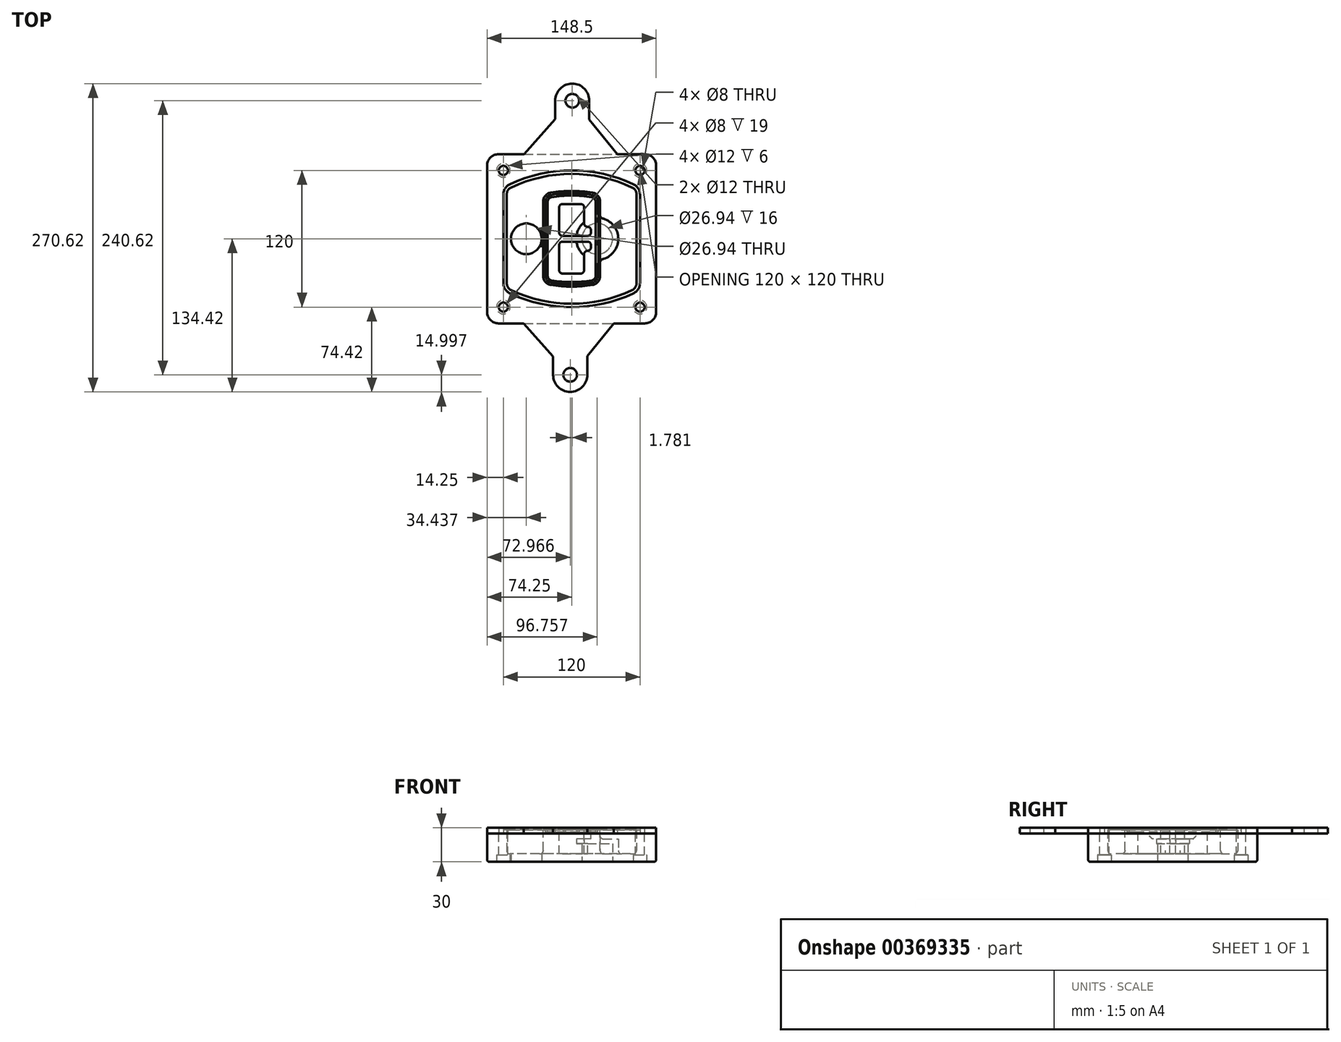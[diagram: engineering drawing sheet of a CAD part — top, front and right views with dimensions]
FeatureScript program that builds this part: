
annotation { "Feature Type Name" : "Feature", "Feature Type Description" : "" }
export const myFeature = defineFeature(function(context is Context, id is Id, definition is map)
    precondition{}
    {
        {
            var Q0;
            Q0=qCreatedBy(makeId("Top.planeOp"),FACE);
            var sketch = newSketch(context, id + "F0", { "sketchPlane" : qUnion([Q0])});
            skPoint(sketch, "E0.rect.middle", {"position": v(0, 0) * mm});
            skLineSegment(sketch, "E1.bottom", {"start": v(-64.25, -74.25) * mm, "end": v(64.25, -74.25) * mm});
            skLineSegment(sketch, "E1.top", {"start": v(-64.25, 74.25) * mm, "end": v(64.25, 74.25) * mm});
            skLineSegment(sketch, "E1.left", {"start": v(-74.25, -64.25) * mm, "end": v(-74.25, 64.25) * mm});
            skLineSegment(sketch, "E1.right", {"start": v(74.25, -64.25) * mm, "end": v(74.25, 64.25) * mm});
            skLineSegment(sketch, "E2", {"start": v(-74.25, 74.25) * mm, "end": v(74.25, -74.25) * mm, "construction": true});
            skLineSegment(sketch, "E3", {"start": v(74.25, 74.25) * mm, "end": v(-74.25, -74.25) * mm, "construction": true});
            skCircle(sketch, "E4", {"center": v(-60, 60) * mm, "radius": 4 * mm});
            skCircle(sketch, "E5", {"center": v(60, 60) * mm, "radius": 4 * mm});
            skCircle(sketch, "E6", {"center": v(60, -60) * mm, "radius": 4 * mm});
            skCircle(sketch, "E7", {"center": v(-60, -60) * mm, "radius": 4 * mm});
            skLineSegment(sketch, "E8", {"start": v(-60, 60) * mm, "end": v(60, 60) * mm, "construction": true});
            skLineSegment(sketch, "E9", {"start": v(60, 60) * mm, "end": v(60, -60) * mm, "construction": true});
            skLineSegment(sketch, "E10", {"start": v(60, -60) * mm, "end": v(-60, -60) * mm, "construction": true});
            skLineSegment(sketch, "E11", {"start": v(-60, -60) * mm, "end": v(-60, 60) * mm, "construction": true});
            skLineSegment(sketch, "E12", {"start": v(-60, 38.83) * mm, "end": v(-60, -38.83) * mm});
            skLineSegment(sketch, "E13", {"start": v(60, 38.83) * mm, "end": v(60, -38.83) * mm});
            skArc(sketch, "E14", {"start": v(54.26, 47.88) * mm, "mid": v(0, 60) * mm, "end": v(-54.26, 47.88) * mm});
            skArc(sketch, "E15", {"start": v(-54.26, -47.88) * mm, "mid": v(0, -60) * mm, "end": v(54.26, -47.88) * mm});
            skLineSegment(sketch, "E16", {"start": v(-60, 0) * mm, "end": v(60, 0) * mm, "construction": true});
            skPoint(sketch, "E17.visualSharp", {"position": v(-60, -45) * mm});
            skArc(sketch, "E17.filletArc", {"start": v(-60, -38.83) * mm, "mid": v(-58.44, -44.2) * mm, "end": v(-54.26, -47.88) * mm});
            skPoint(sketch, "E18.visualSharp", {"position": v(-60, 45) * mm});
            skArc(sketch, "E18.filletArc", {"start": v(-54.26, 47.88) * mm, "mid": v(-58.44, 44.2) * mm, "end": v(-60, 38.83) * mm});
            skPoint(sketch, "E19.visualSharp", {"position": v(60, 45) * mm});
            skArc(sketch, "E19.filletArc", {"start": v(60, 38.83) * mm, "mid": v(58.44, 44.2) * mm, "end": v(54.26, 47.88) * mm});
            skPoint(sketch, "E20.visualSharp", {"position": v(60, -45) * mm});
            skArc(sketch, "E20.filletArc", {"start": v(54.26, -47.88) * mm, "mid": v(58.44, -44.2) * mm, "end": v(60, -38.83) * mm});
            skPoint(sketch, "E21.visualSharp", {"position": v(-74.25, 74.25) * mm});
            skArc(sketch, "E21.filletArc", {"start": v(-64.25, 74.25) * mm, "mid": v(-71.32, 71.32) * mm, "end": v(-74.25, 64.25) * mm});
            skPoint(sketch, "E22.visualSharp", {"position": v(74.25, 74.25) * mm});
            skArc(sketch, "E22.filletArc", {"start": v(74.25, 64.25) * mm, "mid": v(71.32, 71.32) * mm, "end": v(64.25, 74.25) * mm});
            skPoint(sketch, "E23.visualSharp", {"position": v(74.25, -74.25) * mm});
            skArc(sketch, "E23.filletArc", {"start": v(64.25, -74.25) * mm, "mid": v(71.32, -71.32) * mm, "end": v(74.25, -64.25) * mm});
            skPoint(sketch, "E24.visualSharp", {"position": v(-74.25, -74.25) * mm});
            skArc(sketch, "E24.filletArc", {"start": v(-74.25, -64.25) * mm, "mid": v(-71.32, -71.32) * mm, "end": v(-64.25, -74.25) * mm});
            skArc(sketch, "E25.0", {"start": v(57, 38.83) * mm, "mid": v(55.9, 42.58) * mm, "end": v(52.98, 45.17) * mm});
            skLineSegment(sketch, "E25.1", {"start": v(57, 38.83) * mm, "end": v(57, -38.83) * mm});
            skArc(sketch, "E25.2", {"start": v(52.98, -45.17) * mm, "mid": v(55.9, -42.58) * mm, "end": v(57, -38.83) * mm});
            skArc(sketch, "E25.3", {"start": v(-52.98, -45.17) * mm, "mid": v(0, -57) * mm, "end": v(52.98, -45.17) * mm});
            skArc(sketch, "E25.4", {"start": v(-57, -38.83) * mm, "mid": v(-55.9, -42.58) * mm, "end": v(-52.98, -45.17) * mm});
            skArc(sketch, "E25.5", {"start": v(52.98, 45.17) * mm, "mid": v(0, 57) * mm, "end": v(-52.98, 45.17) * mm});
            skLineSegment(sketch, "E25.6", {"start": v(-57, 38.83) * mm, "end": v(-57, -38.83) * mm});
            skArc(sketch, "E25.7", {"start": v(-52.98, 45.17) * mm, "mid": v(-55.9, 42.58) * mm, "end": v(-57, 38.83) * mm});
            skArc(sketch, "E26.0", {"start": v(-55.96, 51.5) * mm, "mid": v(-61.82, 46.33) * mm, "end": v(-64, 38.83) * mm});
            skArc(sketch, "E26.1", {"start": v(55.96, 51.5) * mm, "mid": v(0, 64) * mm, "end": v(-55.96, 51.5) * mm});
            skArc(sketch, "E26.2", {"start": v(64, 38.83) * mm, "mid": v(61.82, 46.33) * mm, "end": v(55.96, 51.5) * mm});
            skLineSegment(sketch, "E26.3", {"start": v(64, 38.83) * mm, "end": v(64, -38.83) * mm});
            skArc(sketch, "E26.4", {"start": v(55.96, -51.5) * mm, "mid": v(61.82, -46.33) * mm, "end": v(64, -38.83) * mm});
            skLineSegment(sketch, "E26.5", {"start": v(-64, 38.83) * mm, "end": v(-64, -38.83) * mm});
            skArc(sketch, "E26.6", {"start": v(-55.96, -51.5) * mm, "mid": v(0, -64) * mm, "end": v(55.96, -51.5) * mm});
            skArc(sketch, "E26.7", {"start": v(-64, -38.83) * mm, "mid": v(-61.82, -46.33) * mm, "end": v(-55.96, -51.5) * mm});
            skSolve(sketch);
        }
        {
            var Q0;
            Q0=makeQuery(id+"F0.imprint","IMPRINT",FACE,{"disambiguationData":[TD([[makeQuery(id+"F0.imprint","IMPRINT",EDGE,{"derivedFrom":sQuery(id+"F0.wireOp",EDGE,"E1.bottom")}),1.0]])]});
            var Q1;
            Q1=makeQuery(id+"F0.imprint","IMPRINT",FACE,{"disambiguationData":[TD([[makeQuery(id+"F0.imprint","IMPRINT",EDGE,{"derivedFrom":sQuery(id+"F0.wireOp",EDGE,"E12")}),1.0]])]});
            var Q2;
            Q2=makeQuery(id+"F0.imprint","IMPRINT",FACE,{"disambiguationData":[TD([[makeQuery(id+"F0.imprint","IMPRINT",EDGE,{"derivedFrom":sQuery(id+"F0.wireOp",EDGE,"E25.0")}),1.0]])]});
            var Q3;
            Q3=makeQuery(id+"F0.imprint","IMPRINT",FACE,{"disambiguationData":[TD([[makeQuery(id+"F0.imprint","IMPRINT",EDGE,{"derivedFrom":sQuery(id+"F0.wireOp",EDGE,"E12")}),-1.0]])]});
            extrude(context, id + "F1", {"entities" : qUnion([Q0, Q1, Q2, Q3]), "oppositeDirection" : true, "depth" : 25 * mm});
        }
        {
            var Q0;
            Q0=makeQuery(id+"F0.imprint","IMPRINT",FACE,{"disambiguationData":[TD([[makeQuery(id+"F0.imprint","IMPRINT",EDGE,{"derivedFrom":sQuery(id+"F0.wireOp",EDGE,"E12")}),1.0]])]});
            extrude(context, id + "F2", {"entities" : qUnion([Q0]), "operationType" : NewBodyOperationType.ADD, "depth" : 3 * mm});
        }
        {
            var Q0;
            Q0=makeQuery(id+"F0.imprint","IMPRINT",FACE,{"disambiguationData":[TD([[makeQuery(id+"F0.imprint","IMPRINT",EDGE,{"derivedFrom":sQuery(id+"F0.wireOp",EDGE,"E25.0")}),1.0]])]});
            extrude(context, id + "F3", {"entities" : qUnion([Q0]), "operationType" : NewBodyOperationType.REMOVE, "oppositeDirection" : true, "depth" : 18 * mm});
        }
        {
            var Q0;
            Q0=makeQuery(id+"F2.opExtrude","CAP_FACE",FACE,{"disambiguationData":[OSD([sQuery(id+"F0.wireOp",EDGE,"E12"),sQuery(id+"F0.wireOp",EDGE,"E13"),sQuery(id+"F0.wireOp",EDGE,"E14"),sQuery(id+"F0.wireOp",EDGE,"E15"),sQuery(id+"F0.wireOp",EDGE,"E17.filletArc"),sQuery(id+"F0.wireOp",EDGE,"E18.filletArc"),sQuery(id+"F0.wireOp",EDGE,"E19.filletArc"),sQuery(id+"F0.wireOp",EDGE,"E20.filletArc"),sQuery(id+"F0.wireOp",EDGE,"E25.0"),sQuery(id+"F0.wireOp",EDGE,"E25.1"),sQuery(id+"F0.wireOp",EDGE,"E25.2"),sQuery(id+"F0.wireOp",EDGE,"E25.3"),sQuery(id+"F0.wireOp",EDGE,"E25.4"),sQuery(id+"F0.wireOp",EDGE,"E25.5"),sQuery(id+"F0.wireOp",EDGE,"E25.6"),sQuery(id+"F0.wireOp",EDGE,"E25.7")])],"isStart":false});
            var sketch = newSketch(context, id + "F4", { "sketchPlane" : qUnion([Q0])});
            skArc(sketch, "E27.0", {"start": v(-18.34, -40.45) * mm, "mid": v(0, -42) * mm, "end": v(18.34, -40.45) * mm});
            skArc(sketch, "E28.0", {"start": v(18.34, 40.45) * mm, "mid": v(0, 42) * mm, "end": v(-18.34, 40.45) * mm});
            skLineSegment(sketch, "E29", {"start": v(-25, 32.57) * mm, "end": v(-25, -32.57) * mm});
            skLineSegment(sketch, "E30", {"start": v(25, 32.57) * mm, "end": v(25, -32.57) * mm});
            skLineSegment(sketch, "E31", {"start": v(-25, 39.1) * mm, "end": v(25, 39.1) * mm, "construction": true});
            skLineSegment(sketch, "E32", {"start": v(-25, -39.1) * mm, "end": v(25, -39.1) * mm, "construction": true});
            skPoint(sketch, "E33.visualSharp", {"position": v(-25, 39.1) * mm});
            skArc(sketch, "E33.filletArc", {"start": v(-18.34, 40.45) * mm, "mid": v(-23.11, 37.73) * mm, "end": v(-25, 32.57) * mm});
            skPoint(sketch, "E34.visualSharp", {"position": v(25, 39.1) * mm});
            skArc(sketch, "E34.filletArc", {"start": v(25, 32.57) * mm, "mid": v(23.11, 37.73) * mm, "end": v(18.34, 40.45) * mm});
            skPoint(sketch, "E35.visualSharp", {"position": v(25, -39.1) * mm});
            skArc(sketch, "E35.filletArc", {"start": v(18.34, -40.45) * mm, "mid": v(23.11, -37.73) * mm, "end": v(25, -32.57) * mm});
            skPoint(sketch, "E36.visualSharp", {"position": v(-25, -39.1) * mm});
            skArc(sketch, "E36.filletArc", {"start": v(-25, -32.57) * mm, "mid": v(-23.11, -37.73) * mm, "end": v(-18.34, -40.45) * mm});
            skArc(sketch, "E37.0", {"start": v(52.98, 45.17) * mm, "mid": v(0, 57) * mm, "end": v(-52.98, 45.17) * mm});
            skArc(sketch, "E37.1", {"start": v(-52.98, 45.17) * mm, "mid": v(-55.9, 42.58) * mm, "end": v(-57, 38.83) * mm});
            skLineSegment(sketch, "E37.2", {"start": v(-57, 38.83) * mm, "end": v(-57, -38.83) * mm});
            skArc(sketch, "E37.3", {"start": v(-57, -38.83) * mm, "mid": v(-55.9, -42.58) * mm, "end": v(-52.98, -45.17) * mm});
            skArc(sketch, "E37.4", {"start": v(-52.98, -45.17) * mm, "mid": v(0, -57) * mm, "end": v(52.98, -45.17) * mm});
            skArc(sketch, "E37.5", {"start": v(52.98, -45.17) * mm, "mid": v(55.9, -42.58) * mm, "end": v(57, -38.83) * mm});
            skLineSegment(sketch, "E37.6", {"start": v(57, 38.83) * mm, "end": v(57, -38.83) * mm});
            skArc(sketch, "E37.7", {"start": v(57, 38.83) * mm, "mid": v(55.9, 42.58) * mm, "end": v(52.98, 45.17) * mm});
            skLineSegment(sketch, "E38.0", {"start": v(23, 32.57) * mm, "end": v(23, -32.57) * mm});
            skArc(sketch, "E38.1", {"start": v(18, -38.48) * mm, "mid": v(21.58, -36.44) * mm, "end": v(23, -32.57) * mm});
            skArc(sketch, "E38.2", {"start": v(-18, -38.48) * mm, "mid": v(0, -40) * mm, "end": v(18, -38.48) * mm});
            skArc(sketch, "E38.3", {"start": v(-23, -32.57) * mm, "mid": v(-21.58, -36.44) * mm, "end": v(-18, -38.48) * mm});
            skLineSegment(sketch, "E38.4", {"start": v(-23, 32.57) * mm, "end": v(-23, -32.57) * mm});
            skArc(sketch, "E38.5", {"start": v(23, 32.57) * mm, "mid": v(21.58, 36.44) * mm, "end": v(18, 38.48) * mm});
            skArc(sketch, "E38.6", {"start": v(-18, 38.48) * mm, "mid": v(-21.58, 36.44) * mm, "end": v(-23, 32.57) * mm});
            skArc(sketch, "E38.7", {"start": v(18, 38.48) * mm, "mid": v(0, 40) * mm, "end": v(-18, 38.48) * mm});
            skArc(sketch, "E39.0", {"start": v(21, 32.57) * mm, "mid": v(20.06, 35.15) * mm, "end": v(17.67, 36.5) * mm});
            skLineSegment(sketch, "E39.1", {"start": v(21, 32.57) * mm, "end": v(21, -32.57) * mm});
            skArc(sketch, "E39.2", {"start": v(17.67, -36.5) * mm, "mid": v(20.06, -35.15) * mm, "end": v(21, -32.57) * mm});
            skArc(sketch, "E39.3", {"start": v(-17.67, -36.5) * mm, "mid": v(0, -38) * mm, "end": v(17.67, -36.5) * mm});
            skArc(sketch, "E39.4", {"start": v(-21, -32.57) * mm, "mid": v(-20.06, -35.15) * mm, "end": v(-17.67, -36.5) * mm});
            skArc(sketch, "E39.5", {"start": v(17.67, 36.5) * mm, "mid": v(0, 38) * mm, "end": v(-17.67, 36.5) * mm});
            skLineSegment(sketch, "E39.6", {"start": v(-21, 32.57) * mm, "end": v(-21, -32.57) * mm});
            skArc(sketch, "E39.7", {"start": v(-17.67, 36.5) * mm, "mid": v(-20.06, 35.15) * mm, "end": v(-21, 32.57) * mm});
            skLineSegment(sketch, "E40", {"start": v(-25, 0) * mm, "end": v(25, 0) * mm, "construction": true});
            skLineSegment(sketch, "E41", {"start": v(-11, 5.5) * mm, "end": v(-11, 27.5) * mm});
            skLineSegment(sketch, "E42", {"start": v(-8, 30.5) * mm, "end": v(8, 30.5) * mm});
            skLineSegment(sketch, "E43", {"start": v(11, 27.5) * mm, "end": v(11, 13.5) * mm});
            skLineSegment(sketch, "E44", {"start": v(14, 10.5) * mm, "end": v(14, 10.5) * mm});
            skLineSegment(sketch, "E45", {"start": v(17, 7.5) * mm, "end": v(17, 5.5) * mm});
            skLineSegment(sketch, "E46", {"start": v(14, 2.5) * mm, "end": v(-8, 2.5) * mm});
            skPoint(sketch, "E47.visualSharp", {"position": v(-11, 30.5) * mm});
            skArc(sketch, "E47.filletArc", {"start": v(-8, 30.5) * mm, "mid": v(-10.12, 29.62) * mm, "end": v(-11, 27.5) * mm});
            skPoint(sketch, "E48.visualSharp", {"position": v(11, 30.5) * mm});
            skArc(sketch, "E48.filletArc", {"start": v(11, 27.5) * mm, "mid": v(10.12, 29.62) * mm, "end": v(8, 30.5) * mm});
            skPoint(sketch, "E49.visualSharp", {"position": v(11, 10.5) * mm});
            skArc(sketch, "E49.filletArc", {"start": v(11, 13.5) * mm, "mid": v(11.88, 11.38) * mm, "end": v(14, 10.5) * mm});
            skPoint(sketch, "E50.visualSharp", {"position": v(17, 10.5) * mm});
            skArc(sketch, "E50.filletArc", {"start": v(17, 7.5) * mm, "mid": v(16.12, 9.62) * mm, "end": v(14, 10.5) * mm});
            skPoint(sketch, "E51.visualSharp", {"position": v(17, 2.5) * mm});
            skArc(sketch, "E51.filletArc", {"start": v(14, 2.5) * mm, "mid": v(16.12, 3.38) * mm, "end": v(17, 5.5) * mm});
            skPoint(sketch, "E52.visualSharp", {"position": v(-11, 2.5) * mm});
            skArc(sketch, "E52.filletArc", {"start": v(-11, 5.5) * mm, "mid": v(-10.12, 3.38) * mm, "end": v(-8, 2.5) * mm});
            skLineSegment(sketch, "E53.0.MirrorCS", {"start": v(14, -2.5) * mm, "end": v(-8, -2.5) * mm});
            skArc(sketch, "E54.0.MirrorCS", {"start": v(-11, -5.5) * mm, "mid": v(-10.12, -3.38) * mm, "end": v(-8, -2.5) * mm});
            skLineSegment(sketch, "E55.0.MirrorCS", {"start": v(-11, -5.5) * mm, "end": v(-11, -27.5) * mm});
            skArc(sketch, "E56.0.MirrorCS", {"start": v(-8, -30.5) * mm, "mid": v(-10.12, -29.62) * mm, "end": v(-11, -27.5) * mm});
            skLineSegment(sketch, "E57.0.MirrorCS", {"start": v(-8, -30.5) * mm, "end": v(8, -30.5) * mm});
            skArc(sketch, "E58.0.MirrorCS", {"start": v(11, -27.5) * mm, "mid": v(10.12, -29.62) * mm, "end": v(8, -30.5) * mm});
            skLineSegment(sketch, "E59.0.MirrorCS", {"start": v(11, -27.5) * mm, "end": v(11, -13.5) * mm});
            skArc(sketch, "E60.0.MirrorCS", {"start": v(11, -13.5) * mm, "mid": v(11.88, -11.38) * mm, "end": v(14, -10.5) * mm});
            skArc(sketch, "E61.0.MirrorCS", {"start": v(17, -7.5) * mm, "mid": v(16.12, -9.62) * mm, "end": v(14, -10.5) * mm});
            skLineSegment(sketch, "E62.0.MirrorCS", {"start": v(17, -7.5) * mm, "end": v(17, -5.5) * mm});
            skArc(sketch, "E63.0.MirrorCS", {"start": v(14, -2.5) * mm, "mid": v(16.12, -3.38) * mm, "end": v(17, -5.5) * mm});
            skSolve(sketch);
        }
        {
            var Q0;
            Q0=makeQuery(id+"F4.imprint","IMPRINT",FACE,{"disambiguationData":[TD([[makeQuery(id+"F4.imprint","IMPRINT",EDGE,{"derivedFrom":sQuery(id+"F4.wireOp",EDGE,"E27.0")}),1.0]])]});
            var Q1;
            Q1=makeQuery(id+"F4.imprint","IMPRINT",FACE,{"disambiguationData":[TD([[makeQuery(id+"F4.imprint","IMPRINT",EDGE,{"derivedFrom":sQuery(id+"F4.wireOp",EDGE,"E38.0")}),-1.0]])]});
            var Q2;
            Q2=makeQuery(id+"F4.imprint","IMPRINT",FACE,{"disambiguationData":[TD([[makeQuery(id+"F4.imprint","IMPRINT",EDGE,{"derivedFrom":sQuery(id+"F4.wireOp",EDGE,"E39.0")}),1.0]])]});
            extrude(context, id + "F5", {"entities" : qUnion([Q0, Q1, Q2]), "operationType" : NewBodyOperationType.ADD, "endBound" : BoundingType.UP_TO_NEXT, "oppositeDirection" : true, "depth" : 25 * mm});
        }
        {
            var Q0;
            Q0=makeQuery(id+"F4.imprint","IMPRINT",FACE,{"disambiguationData":[TD([[makeQuery(id+"F4.imprint","IMPRINT",EDGE,{"derivedFrom":sQuery(id+"F4.wireOp",EDGE,"E38.0")}),-1.0]])]});
            extrude(context, id + "F6", {"entities" : qUnion([Q0]), "operationType" : NewBodyOperationType.REMOVE, "oppositeDirection" : true, "depth" : 2 * mm});
        }
        {
            var Q0;
            Q0=makeQuery(id+"F1.opExtrude","CAP_FACE",FACE,{"disambiguationData":[OSD([sQuery(id+"F0.wireOp",EDGE,"E1.bottom"),sQuery(id+"F0.wireOp",EDGE,"E1.top"),sQuery(id+"F0.wireOp",EDGE,"E1.left"),sQuery(id+"F0.wireOp",EDGE,"E1.right"),sQuery(id+"F0.wireOp",EDGE,"E4"),sQuery(id+"F0.wireOp",EDGE,"E5"),sQuery(id+"F0.wireOp",EDGE,"E6"),sQuery(id+"F0.wireOp",EDGE,"E7"),sQuery(id+"F0.wireOp",EDGE,"E21.filletArc"),sQuery(id+"F0.wireOp",EDGE,"E22.filletArc"),sQuery(id+"F0.wireOp",EDGE,"E23.filletArc"),sQuery(id+"F0.wireOp",EDGE,"E24.filletArc")])],"isStart":false});
            var sketch = newSketch(context, id + "F7", { "sketchPlane" : qUnion([Q0])});
            skCircle(sketch, "E64", {"center": v(22.5, 0) * mm, "radius": 13.47 * mm});
            skCircle(sketch, "E65", {"center": v(-39.81, 0) * mm, "radius": 13.47 * mm});
            skLineSegment(sketch, "E66", {"start": v(74.25, 0) * mm, "end": v(-74.25, 0) * mm});
            skCircle(sketch, "E67", {"center": v(22.5, 0) * mm, "radius": 18.47 * mm});
            skCircle(sketch, "E68", {"center": v(60, -60) * mm, "radius": 6 * mm});
            skCircle(sketch, "E69", {"center": v(-60, -60) * mm, "radius": 6 * mm});
            skCircle(sketch, "E70", {"center": v(-60, 60) * mm, "radius": 6 * mm});
            skCircle(sketch, "E71", {"center": v(60, 60) * mm, "radius": 6 * mm});
            skSolve(sketch);
        }
        {
            var Q0;
            {var subQ1=sQuery(id+"F7.wireOp",EDGE,"E66");var subQ4=sQuery(id+"F7.wireOp",EDGE,"E64");var subQ6=makeQuery(id+"F7.imprint","INTERSECT",VERTEX,{"disambiguationData":[OD(0.0)],"derivedFrom":[subQ4,subQ1]});Q0=makeQuery(id+"F7.imprint","IMPRINT",FACE,{"disambiguationData":[TD([[makeQuery(id+"F7.imprint","IMPRINT",EDGE,{"disambiguationData":[TD([[subQ6,-1.0]])],"derivedFrom":subQ4}),-1.0]])]});}
            var Q1;
            {var subQ0=sQuery(id+"F7.wireOp",EDGE,"E66");var subQ1=sQuery(id+"F7.wireOp",EDGE,"E64");var subQ3=makeQuery(id+"F7.imprint","INTERSECT",VERTEX,{"disambiguationData":[OD(0.0)],"derivedFrom":[subQ1,subQ0]});Q1=makeQuery(id+"F7.imprint","IMPRINT",FACE,{"disambiguationData":[TD([[makeQuery(id+"F7.imprint","IMPRINT",EDGE,{"disambiguationData":[TD([[subQ3,-1.0]])],"derivedFrom":subQ1}),1.0]])]});}
            var Q2;
            {var subQ0=sQuery(id+"F7.wireOp",EDGE,"E66");var subQ1=sQuery(id+"F7.wireOp",EDGE,"E64");var subQ3=makeQuery(id+"F7.imprint","INTERSECT",VERTEX,{"disambiguationData":[OD(0.0)],"derivedFrom":[subQ1,subQ0]});Q2=makeQuery(id+"F7.imprint","IMPRINT",FACE,{"disambiguationData":[TD([[makeQuery(id+"F7.imprint","IMPRINT",EDGE,{"disambiguationData":[TD([[subQ3,1.0]])],"derivedFrom":subQ1}),1.0]])]});}
            var Q3;
            {var subQ1=sQuery(id+"F7.wireOp",EDGE,"E66");var subQ4=sQuery(id+"F7.wireOp",EDGE,"E64");var subQ6=makeQuery(id+"F7.imprint","INTERSECT",VERTEX,{"disambiguationData":[OD(0.0)],"derivedFrom":[subQ4,subQ1]});Q3=makeQuery(id+"F7.imprint","IMPRINT",FACE,{"disambiguationData":[TD([[makeQuery(id+"F7.imprint","IMPRINT",EDGE,{"disambiguationData":[TD([[subQ6,1.0]])],"derivedFrom":subQ4}),-1.0]])]});}
            extrude(context, id + "F8", {"entities" : qUnion([Q0, Q1, Q2, Q3]), "operationType" : NewBodyOperationType.ADD, "oppositeDirection" : true, "depth" : 20 * mm});
        }
        {
            var Q0;
            {var subQ0=sQuery(id+"F7.wireOp",EDGE,"E66");var subQ1=sQuery(id+"F7.wireOp",EDGE,"E64");var subQ3=makeQuery(id+"F7.imprint","INTERSECT",VERTEX,{"disambiguationData":[OD(0.0)],"derivedFrom":[subQ1,subQ0]});Q0=makeQuery(id+"F7.imprint","IMPRINT",FACE,{"disambiguationData":[TD([[makeQuery(id+"F7.imprint","IMPRINT",EDGE,{"disambiguationData":[TD([[subQ3,-1.0]])],"derivedFrom":subQ1}),1.0]])]});}
            var Q1;
            {var subQ0=sQuery(id+"F7.wireOp",EDGE,"E66");var subQ1=sQuery(id+"F7.wireOp",EDGE,"E64");var subQ3=makeQuery(id+"F7.imprint","INTERSECT",VERTEX,{"disambiguationData":[OD(0.0)],"derivedFrom":[subQ1,subQ0]});Q1=makeQuery(id+"F7.imprint","IMPRINT",FACE,{"disambiguationData":[TD([[makeQuery(id+"F7.imprint","IMPRINT",EDGE,{"disambiguationData":[TD([[subQ3,1.0]])],"derivedFrom":subQ1}),1.0]])]});}
            extrude(context, id + "F9", {"entities" : qUnion([Q0, Q1]), "operationType" : NewBodyOperationType.REMOVE, "oppositeDirection" : true, "depth" : 16 * mm});
        }
        {
            var Q0;
            {var subQ0=sQuery(id+"F7.wireOp",EDGE,"E66");var subQ1=sQuery(id+"F7.wireOp",EDGE,"E65");var subQ3=makeQuery(id+"F7.imprint","INTERSECT",VERTEX,{"disambiguationData":[OD(0.0)],"derivedFrom":[subQ1,subQ0]});Q0=makeQuery(id+"F7.imprint","IMPRINT",FACE,{"disambiguationData":[TD([[makeQuery(id+"F7.imprint","IMPRINT",EDGE,{"disambiguationData":[TD([[subQ3,-1.0]])],"derivedFrom":subQ1}),1.0]])]});}
            var Q1;
            {var subQ0=sQuery(id+"F7.wireOp",EDGE,"E66");var subQ1=sQuery(id+"F7.wireOp",EDGE,"E65");var subQ3=makeQuery(id+"F7.imprint","INTERSECT",VERTEX,{"disambiguationData":[OD(0.0)],"derivedFrom":[subQ1,subQ0]});Q1=makeQuery(id+"F7.imprint","IMPRINT",FACE,{"disambiguationData":[TD([[makeQuery(id+"F7.imprint","IMPRINT",EDGE,{"disambiguationData":[TD([[subQ3,1.0]])],"derivedFrom":subQ1}),1.0]])]});}
            extrude(context, id + "F10", {"entities" : qUnion([Q0, Q1]), "operationType" : NewBodyOperationType.REMOVE, "oppositeDirection" : true, "depth" : 25 * mm});
        }
        {
            var Q0;
            Q0=makeQuery(id+"F7.imprint","IMPRINT",FACE,{"disambiguationData":[TD([[makeQuery(id+"F7.imprint","IMPRINT",EDGE,{"derivedFrom":sQuery(id+"F7.wireOp",EDGE,"E68")}),1.0]])]});
            var Q1;
            Q1=makeQuery(id+"F7.imprint","IMPRINT",FACE,{"disambiguationData":[TD([[makeQuery(id+"F7.imprint","IMPRINT",EDGE,{"derivedFrom":makeQuery(id+"F1.opExtrude","CAP_EDGE",EDGE,{"disambiguationData":[OSD([sQuery(id+"F0.wireOp",EDGE,"E5")])],"isStart":false})}),-1.0]])]});
            var Q2;
            Q2=makeQuery(id+"F7.imprint","IMPRINT",FACE,{"disambiguationData":[TD([[makeQuery(id+"F7.imprint","IMPRINT",EDGE,{"derivedFrom":sQuery(id+"F7.wireOp",EDGE,"E69")}),1.0]])]});
            var Q3;
            Q3=makeQuery(id+"F7.imprint","IMPRINT",FACE,{"disambiguationData":[TD([[makeQuery(id+"F7.imprint","IMPRINT",EDGE,{"derivedFrom":makeQuery(id+"F1.opExtrude","CAP_EDGE",EDGE,{"disambiguationData":[OSD([sQuery(id+"F0.wireOp",EDGE,"E4")])],"isStart":false})}),-1.0]])]});
            var Q4;
            Q4=makeQuery(id+"F7.imprint","IMPRINT",FACE,{"disambiguationData":[TD([[makeQuery(id+"F7.imprint","IMPRINT",EDGE,{"derivedFrom":sQuery(id+"F7.wireOp",EDGE,"E70")}),1.0]])]});
            var Q5;
            Q5=makeQuery(id+"F7.imprint","IMPRINT",FACE,{"disambiguationData":[TD([[makeQuery(id+"F7.imprint","IMPRINT",EDGE,{"derivedFrom":makeQuery(id+"F1.opExtrude","CAP_EDGE",EDGE,{"disambiguationData":[OSD([sQuery(id+"F0.wireOp",EDGE,"E7")])],"isStart":false})}),-1.0]])]});
            var Q6;
            Q6=makeQuery(id+"F7.imprint","IMPRINT",FACE,{"disambiguationData":[TD([[makeQuery(id+"F7.imprint","IMPRINT",EDGE,{"derivedFrom":sQuery(id+"F7.wireOp",EDGE,"E71")}),1.0]])]});
            var Q7;
            Q7=makeQuery(id+"F7.imprint","IMPRINT",FACE,{"disambiguationData":[TD([[makeQuery(id+"F7.imprint","IMPRINT",EDGE,{"derivedFrom":makeQuery(id+"F1.opExtrude","CAP_EDGE",EDGE,{"disambiguationData":[OSD([sQuery(id+"F0.wireOp",EDGE,"E6")])],"isStart":false})}),-1.0]])]});
            extrude(context, id + "F11", {"entities" : qUnion([Q0, Q1, Q2, Q3, Q4, Q5, Q6, Q7]), "operationType" : NewBodyOperationType.REMOVE, "oppositeDirection" : true, "depth" : 6 * mm});
        }
        {
            var Q0;
            Q0=makeQuery(id+"F9.boolean.opBoolean","COPY",FACE,{"derivedFrom":makeQuery(id+"F9.opExtrude","CAP_FACE",FACE,{"disambiguationData":[OSD([sQuery(id+"F7.wireOp",EDGE,"E64")])],"isStart":false})});
            var sketch = newSketch(context, id + "F12", { "sketchPlane" : qUnion([Q0])});
            skArc(sketch, "E72.0", {"start": v(11, 14.45) * mm, "mid": v(6.45, 9.13) * mm, "end": v(4.2, 2.5) * mm});
            skArc(sketch, "E72.1", {"start": v(4.2, -2.5) * mm, "mid": v(6.45, -9.13) * mm, "end": v(11, -14.45) * mm});
            skLineSegment(sketch, "E73", {"start": v(4.2, -2.5) * mm, "end": v(14, -2.5) * mm});
            skLineSegment(sketch, "E74.0", {"start": v(14, 2.5) * mm, "end": v(4.2, 2.5) * mm});
            skArc(sketch, "E74.1", {"start": v(14, 2.5) * mm, "mid": v(16.12, 3.38) * mm, "end": v(17, 5.5) * mm});
            skLineSegment(sketch, "E74.2", {"start": v(17, 7.5) * mm, "end": v(17, 5.5) * mm});
            skArc(sketch, "E74.3", {"start": v(17, 7.5) * mm, "mid": v(16.12, 9.62) * mm, "end": v(14, 10.5) * mm});
            skArc(sketch, "E74.4", {"start": v(11, 13.5) * mm, "mid": v(11.88, 11.38) * mm, "end": v(14, 10.5) * mm});
            skLineSegment(sketch, "E74.5", {"start": v(11, 14.45) * mm, "end": v(11, 13.5) * mm});
            skLineSegment(sketch, "E74.7", {"start": v(14, -2.5) * mm, "end": v(4.2, -2.5) * mm});
            skArc(sketch, "E74.8", {"start": v(14, -2.5) * mm, "mid": v(16.12, -3.38) * mm, "end": v(17, -5.5) * mm});
            skLineSegment(sketch, "E74.9", {"start": v(17, -7.5) * mm, "end": v(17, -5.5) * mm});
            skArc(sketch, "E74.10", {"start": v(17, -7.5) * mm, "mid": v(16.12, -9.62) * mm, "end": v(14, -10.5) * mm});
            skArc(sketch, "E74.11", {"start": v(11, -13.5) * mm, "mid": v(11.88, -11.38) * mm, "end": v(14, -10.5) * mm});
            skLineSegment(sketch, "E74.12", {"start": v(11, -14.45) * mm, "end": v(11, -13.5) * mm});
            skPoint(sketch, "E75.orphan", {"position": v(11, -27.5) * mm});
            skPoint(sketch, "E76.orphan", {"position": v(-8, -2.5) * mm});
            skPoint(sketch, "E77.orphan", {"position": v(-8, 2.5) * mm});
            skPoint(sketch, "E78.orphan", {"position": v(11, 27.5) * mm});
            skSolve(sketch);
        }
        {
            var Q0;
            {var subQ7=sQuery(id+"F12.wireOp",EDGE,"E72.0");var subQ14=sQuery(id+"F12.wireOp",EDGE,"E72.1");var subQ16=sQuery(id+"F12.wireOp",EDGE,"E74.1");var subQ18=sQuery(id+"F12.wireOp",EDGE,"E74.8");Q0=qUnion([makeQuery(id+"F12.imprint","IMPRINT",FACE,{"disambiguationData":[TD([[makeQuery(id+"F12.imprint","IMPRINT",EDGE,{"derivedFrom":subQ7}),1.0]])]}),makeQuery(id+"F12.imprint","IMPRINT",FACE,{"disambiguationData":[TD([[makeQuery(id+"F12.imprint","IMPRINT",EDGE,{"derivedFrom":subQ14}),1.0]])]}),makeQuery(id+"F12.imprint","IMPRINT",FACE,{"disambiguationData":[TD([[makeQuery(id+"F12.imprint","IMPRINT",EDGE,{"derivedFrom":subQ16}),1.0]])]}),makeQuery(id+"F12.imprint","IMPRINT",FACE,{"disambiguationData":[TD([[makeQuery(id+"F12.imprint","IMPRINT",EDGE,{"derivedFrom":subQ18}),-1.0]])]})]);}
            var Q1;
            Q1=makeQuery(id+"F5.boolean.opBoolean","SPLIT",FACE,{"disambiguationData":[TD([makeQuery(id+"F5.opExtrude","SWEPT_FACE",FACE,{"disambiguationData":[OSD([sQuery(id+"F4.wireOp",EDGE,"E41")])]})])],"derivedFrom":makeQuery(id+"F3.boolean.opBoolean","COPY",FACE,{"derivedFrom":makeQuery(id+"F3.opExtrude","CAP_FACE",FACE,{"disambiguationData":[OSD([sQuery(id+"F0.wireOp",EDGE,"E25.0"),sQuery(id+"F0.wireOp",EDGE,"E25.1"),sQuery(id+"F0.wireOp",EDGE,"E25.2"),sQuery(id+"F0.wireOp",EDGE,"E25.3"),sQuery(id+"F0.wireOp",EDGE,"E25.4"),sQuery(id+"F0.wireOp",EDGE,"E25.5"),sQuery(id+"F0.wireOp",EDGE,"E25.6"),sQuery(id+"F0.wireOp",EDGE,"E25.7")])],"isStart":false})})});
            extrude(context, id + "F13", {"entities" : qUnion([Q0]), "operationType" : NewBodyOperationType.REMOVE, "endBound" : BoundingType.UP_TO_SURFACE, "endBoundEntityFace" : qUnion([Q1]), "depth" : 25 * mm});
        }
        {
            var Q0;
            Q0=makeQuery(id+"F3.boolean.opBoolean","COPY",EDGE,{"derivedFrom":makeQuery(id+"F3.opExtrude","CAP_EDGE",EDGE,{"disambiguationData":[OSD([sQuery(id+"F0.wireOp",EDGE,"E25.6")])],"isStart":false})});
            var Q1;
            Q1=makeQuery(id+"F8.boolean.opBoolean","INTERSECT",EDGE,{"derivedFrom":[makeQuery(id+"F5.opExtrude","SWEPT_FACE",FACE,{"disambiguationData":[OSD([sQuery(id+"F4.wireOp",EDGE,"E30")])]}),makeQuery(id+"F8.opExtrude","CAP_FACE",FACE,{"disambiguationData":[OSD([sQuery(id+"F7.wireOp",EDGE,"E67")])],"isStart":false})]});
            var Q2;
            Q2=makeQuery(id+"F8.boolean.opBoolean","INTERSECT",EDGE,{"disambiguationData":[OD(1.0)],"derivedFrom":[makeQuery(id+"F5.opExtrude","SWEPT_FACE",FACE,{"disambiguationData":[OSD([sQuery(id+"F4.wireOp",EDGE,"E30")])]}),makeQuery(id+"F8.opExtrude","SWEPT_FACE",FACE,{"disambiguationData":[OSD([sQuery(id+"F7.wireOp",EDGE,"E67")])]})]});
            var Q3;
            {var subQ0=sQuery(id+"F4.wireOp",EDGE,"E30");Q3=makeQuery(id+"F8.boolean.opBoolean","SPLIT",EDGE,{"disambiguationData":[TD([makeQuery(id+"F5.opExtrude","SWEPT_FACE",FACE,{"disambiguationData":[OSD([sQuery(id+"F4.wireOp",EDGE,"E35.filletArc")])]})])],"derivedFrom":makeQuery(id+"F5.opExtrude","CAP_EDGE",EDGE,{"disambiguationData":[OSD([subQ0])],"isStart":false})});}
            var Q4;
            {var subQ0=sQuery(id+"F0.wireOp",EDGE,"E25.7");var subQ1=sQuery(id+"F0.wireOp",EDGE,"E25.1");var subQ2=sQuery(id+"F0.wireOp",EDGE,"E25.6");var subQ3=sQuery(id+"F0.wireOp",EDGE,"E25.5");var subQ4=sQuery(id+"F0.wireOp",EDGE,"E25.4");var subQ5=sQuery(id+"F0.wireOp",EDGE,"E25.0");var subQ6=sQuery(id+"F0.wireOp",EDGE,"E25.2");var subQ7=sQuery(id+"F0.wireOp",EDGE,"E25.3");Q4=makeQuery(id+"F8.boolean.opBoolean","INTERSECT",EDGE,{"derivedFrom":[makeQuery(id+"F5.boolean.opBoolean","SPLIT",FACE,{"disambiguationData":[TD([makeQuery(id+"F2.opExtrude","SWEPT_FACE",FACE,{"disambiguationData":[OSD([subQ5])]})])],"derivedFrom":makeQuery(id+"F3.boolean.opBoolean","COPY",FACE,{"derivedFrom":makeQuery(id+"F3.opExtrude","CAP_FACE",FACE,{"disambiguationData":[OSD([subQ5,subQ1,subQ6,subQ7,subQ4,subQ3,subQ2,subQ0])],"isStart":false})})}),makeQuery(id+"F8.opExtrude","SWEPT_FACE",FACE,{"disambiguationData":[OSD([sQuery(id+"F7.wireOp",EDGE,"E67")])]})]});}
            var Q5;
            Q5=makeQuery(id+"F8.boolean.opBoolean","INTERSECT",EDGE,{"disambiguationData":[OD(0.0)],"derivedFrom":[makeQuery(id+"F5.opExtrude","SWEPT_FACE",FACE,{"disambiguationData":[OSD([sQuery(id+"F4.wireOp",EDGE,"E30")])]}),makeQuery(id+"F8.opExtrude","SWEPT_FACE",FACE,{"disambiguationData":[OSD([sQuery(id+"F7.wireOp",EDGE,"E67")])]})]});
            fillet(context, id + "F14", {"entities" : qUnion([Q0, Q1, Q2, Q3, Q4, Q5]), "radius" : 3 * mm, "tangentPropagation" : true, "allowEdgeOverflow" : false});
        }
        {
            var Q0;
            Q0=makeQuery(id+"F1.opExtrude","CAP_EDGE",EDGE,{"disambiguationData":[OSD([sQuery(id+"F0.wireOp",EDGE,"E1.bottom")])],"isStart":false});
            fillet(context, id + "F15", {"entities" : qUnion([Q0]), "radius" : 2 * mm, "tangentPropagation" : true, "allowEdgeOverflow" : false});
        }
        {
            var Q0;
            {var subQ0=sQuery(id+"F0.wireOp",EDGE,"E21.filletArc");var subQ1=sQuery(id+"F0.wireOp",EDGE,"E7");var subQ2=sQuery(id+"F0.wireOp",EDGE,"E6");var subQ3=sQuery(id+"F0.wireOp",EDGE,"E5");var subQ4=sQuery(id+"F0.wireOp",EDGE,"E4");var subQ5=sQuery(id+"F0.wireOp",EDGE,"E22.filletArc");var subQ6=sQuery(id+"F0.wireOp",EDGE,"E1.bottom");var subQ7=sQuery(id+"F0.wireOp",EDGE,"E1.right");var subQ8=sQuery(id+"F0.wireOp",EDGE,"E1.top");var subQ9=sQuery(id+"F0.wireOp",EDGE,"E1.left");var subQ10=sQuery(id+"F0.wireOp",EDGE,"E23.filletArc");var subQ11=sQuery(id+"F0.wireOp",EDGE,"E24.filletArc");Q0=makeQuery(id+"F2.boolean.opBoolean","SPLIT",FACE,{"disambiguationData":[TD([makeQuery(id+"F1.opExtrude","SWEPT_FACE",FACE,{"disambiguationData":[OSD([subQ6])]})])],"derivedFrom":makeQuery(id+"F1.opExtrude","CAP_FACE",FACE,{"disambiguationData":[OSD([subQ6,subQ8,subQ9,subQ7,subQ4,subQ3,subQ2,subQ1,subQ0,subQ5,subQ10,subQ11])],"isStart":true})});}
            var sketch = newSketch(context, id + "F16", { "sketchPlane" : qUnion([Q0])});
            skLineSegment(sketch, "E79", {"start": v(-14.5, 105.14) * mm, "end": v(-41.86, 74.25) * mm});
            skLineSegment(sketch, "E80", {"start": v(-14.5, 105.14) * mm, "end": v(-14.5, 121.2) * mm});
            skLineSegment(sketch, "E81", {"start": v(15.5, 121.2) * mm, "end": v(15.5, 104.84) * mm});
            skArc(sketch, "E82", {"start": v(15.5, 121.2) * mm, "mid": v(0.5, 136.2) * mm, "end": v(-14.5, 121.2) * mm});
            skLineSegment(sketch, "E83", {"start": v(15.5, 104.84) * mm, "end": v(40.19, 74.25) * mm});
            skCircle(sketch, "E84", {"center": v(0.5, 121.2) * mm, "radius": 6 * mm});
            skArc(sketch, "E85.MirrorCS", {"start": v(13.72, -119.42) * mm, "mid": v(-1.28, -134.42) * mm, "end": v(-16.28, -119.42) * mm});
            skLineSegment(sketch, "E86.MirrorCS", {"start": v(13.72, -119.42) * mm, "end": v(13.72, -103.06) * mm});
            skLineSegment(sketch, "E87.MirrorCS", {"start": v(13.72, -103.06) * mm, "end": v(38.4, -72.48) * mm});
            skLineSegment(sketch, "E88.MirrorCS", {"start": v(-16.28, -103.37) * mm, "end": v(-16.28, -119.42) * mm});
            skLineSegment(sketch, "E89.MirrorCS", {"start": v(-16.28, -103.37) * mm, "end": v(-43.64, -72.48) * mm});
            skCircle(sketch, "E90.MirrorC", {"center": v(-1.28, -119.42) * mm, "radius": 6 * mm});
            skSolve(sketch);
        }
        {
            var Q0;
            {var subQ1=sQuery(id+"F16.wireOp",EDGE,"E86.MirrorCS");Q0=makeQuery(id+"F16.imprint","IMPRINT",FACE,{"disambiguationData":[TD([[makeQuery(id+"F16.imprint","IMPRINT",EDGE,{"derivedFrom":subQ1}),1.0]])]});}
            var Q1;
            {var subQ0=sQuery(id+"F16.wireOp",EDGE,"E79");Q1=makeQuery(id+"F16.imprint","IMPRINT",FACE,{"disambiguationData":[TD([[makeQuery(id+"F16.imprint","IMPRINT",EDGE,{"derivedFrom":subQ0}),1.0]])]});}
            var Q2;
            Q2=makeQuery(id+"F16.imprint","IMPRINT",FACE,{"disambiguationData":[TD([[makeQuery(id+"F16.imprint","IMPRINT",EDGE,{"derivedFrom":makeQuery(id+"F1.opExtrude","CAP_EDGE",EDGE,{"disambiguationData":[OSD([sQuery(id+"F0.wireOp",EDGE,"E1.left")])],"isStart":true})}),-1.0]])]});
            var Q3;
            Q3=sQuery(id+"F16.wireOp",EDGE,"E82");
            var Q4;
            Q4=sQuery(id+"F16.wireOp",EDGE,"E84");
            var Q5;
            Q5=sQuery(id+"F16.wireOp",EDGE,"E80");
            var Q6;
            Q6=sQuery(id+"F16.wireOp",EDGE,"E79");
            var Q7;
            Q7=sQuery(id+"F16.wireOp",EDGE,"E81");
            var Q8;
            Q8=sQuery(id+"F16.wireOp",EDGE,"E83");
            var Q9;
            Q9=sQuery(id+"F16.wireOp",EDGE,"E87.MirrorCS");
            var Q10;
            Q10=sQuery(id+"F16.wireOp",EDGE,"E86.MirrorCS");
            var Q11;
            Q11=sQuery(id+"F16.wireOp",EDGE,"E85.MirrorCS");
            var Q12;
            Q12=sQuery(id+"F16.wireOp",EDGE,"E90.MirrorC");
            var Q13;
            Q13=sQuery(id+"F16.wireOp",EDGE,"E88.MirrorCS");
            var Q14;
            Q14=sQuery(id+"F16.wireOp",EDGE,"E89.MirrorCS");
            extrude(context, id + "F17", {"entities" : qUnion([Q0, Q1, Q2]), "surfaceEntities" : qUnion([Q3, Q4, Q5, Q6, Q7, Q8, Q9, Q10, Q11, Q12, Q13, Q14]), "depth" : 5 * mm});
        }
    });
